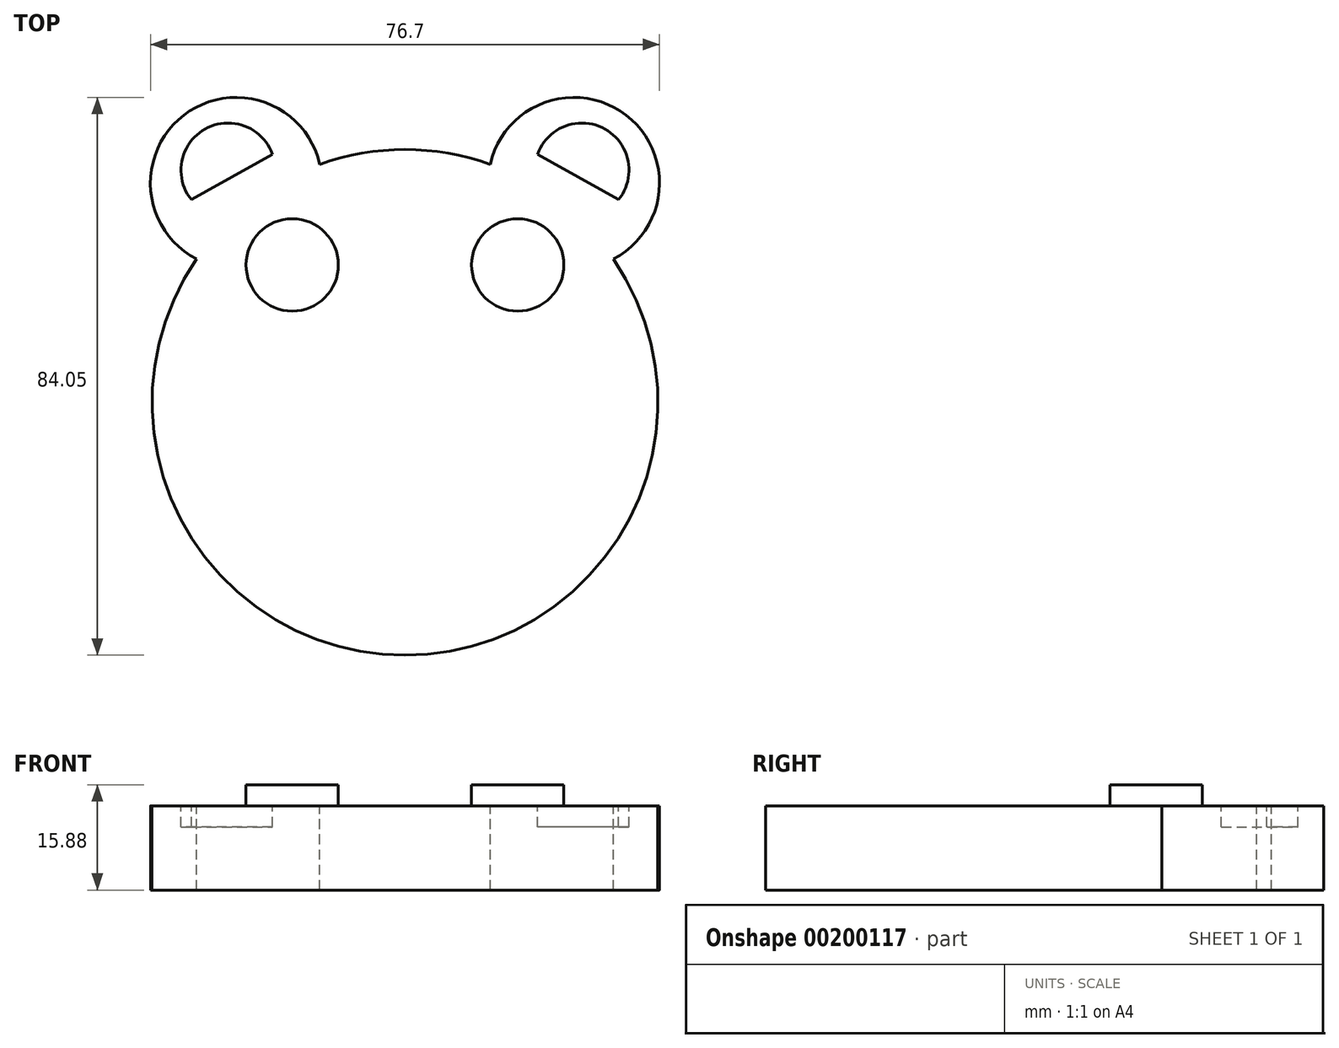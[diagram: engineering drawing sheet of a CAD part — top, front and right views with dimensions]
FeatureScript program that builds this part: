
annotation { "Feature Type Name" : "Feature", "Feature Type Description" : "" }
export const myFeature = defineFeature(function(context is Context, id is Id, definition is map)
    precondition{}
    {
        {
            var Q0;
            Q0=qCreatedBy(makeId("Top.planeOp"),FACE);
            var sketch = newSketch(context, id + "F0", { "sketchPlane" : qUnion([Q0])});
            skCircle(sketch, "E0", {"center": v(0, 0) * mm, "radius": 38.1 * mm});
            skArc(sketch, "E1", {"start": v(-12.85, 35.87) * mm, "mid": v(-33.32, 43.27) * mm, "end": v(-31.4, 21.6) * mm});
            skArc(sketch, "E2.MirrorCS", {"start": v(12.85, 35.87) * mm, "mid": v(33.32, 43.27) * mm, "end": v(31.4, 21.6) * mm});
            skSolve(sketch);
        }
        {
            var Q0;
            Q0 = qSketchRegion(id + "F0", true);
            extrude(context, id + "F1", {"entities" : qUnion([Q0]), "oppositeDirection" : true, "depth" : 12.7 * mm});
        }
        {
            var Q0;
            Q0=makeQuery(id+"F1.opExtrude","CAP_FACE",FACE,{"disambiguationData":[OSD([sQuery(id+"F0.wireOp",EDGE,"E0"),sQuery(id+"F0.wireOp",EDGE,"E1"),sQuery(id+"F0.wireOp",EDGE,"E2.MirrorCS")])],"isStart":true});
            var sketch = newSketch(context, id + "F2", { "sketchPlane" : qUnion([Q0])});
            skCircle(sketch, "E3", {"center": v(-16.99, 20.71) * mm, "radius": 6.96 * mm});
            skCircle(sketch, "E4.MirrorC", {"center": v(16.99, 20.71) * mm, "radius": 6.96 * mm});
            skSolve(sketch);
        }
        {
            var Q0;
            Q0 = qSketchRegion(id + "F2", true);
            extrude(context, id + "F3", {"entities" : qUnion([Q0]), "operationType" : NewBodyOperationType.ADD, "depth" : 3.17 * mm});
        }
        {
            var Q0;
            Q0=makeQuery(id+"F1.opExtrude","CAP_FACE",FACE,{"disambiguationData":[OSD([sQuery(id+"F0.wireOp",EDGE,"E0"),sQuery(id+"F0.wireOp",EDGE,"E1"),sQuery(id+"F0.wireOp",EDGE,"E2.MirrorCS")])],"isStart":true});
            var sketch = newSketch(context, id + "F4", { "sketchPlane" : qUnion([Q0])});
            skArc(sketch, "E5", {"start": v(-19.97, 37.4) * mm, "mid": v(-30.12, 41.18) * mm, "end": v(-32.18, 30.54) * mm});
            skLineSegment(sketch, "E6", {"start": v(-32.18, 30.54) * mm, "end": v(-19.97, 37.4) * mm});
            skArc(sketch, "E7.MirrorCS", {"start": v(19.97, 37.4) * mm, "mid": v(30.12, 41.18) * mm, "end": v(32.18, 30.54) * mm});
            skLineSegment(sketch, "E8.MirrorCS", {"start": v(32.18, 30.54) * mm, "end": v(19.97, 37.4) * mm});
            skSolve(sketch);
        }
        {
            var Q0;
            Q0 = qSketchRegion(id + "F4", true);
            extrude(context, id + "F5", {"entities" : qUnion([Q0]), "operationType" : NewBodyOperationType.REMOVE, "oppositeDirection" : true, "depth" : 3.17 * mm});
        }
    });
